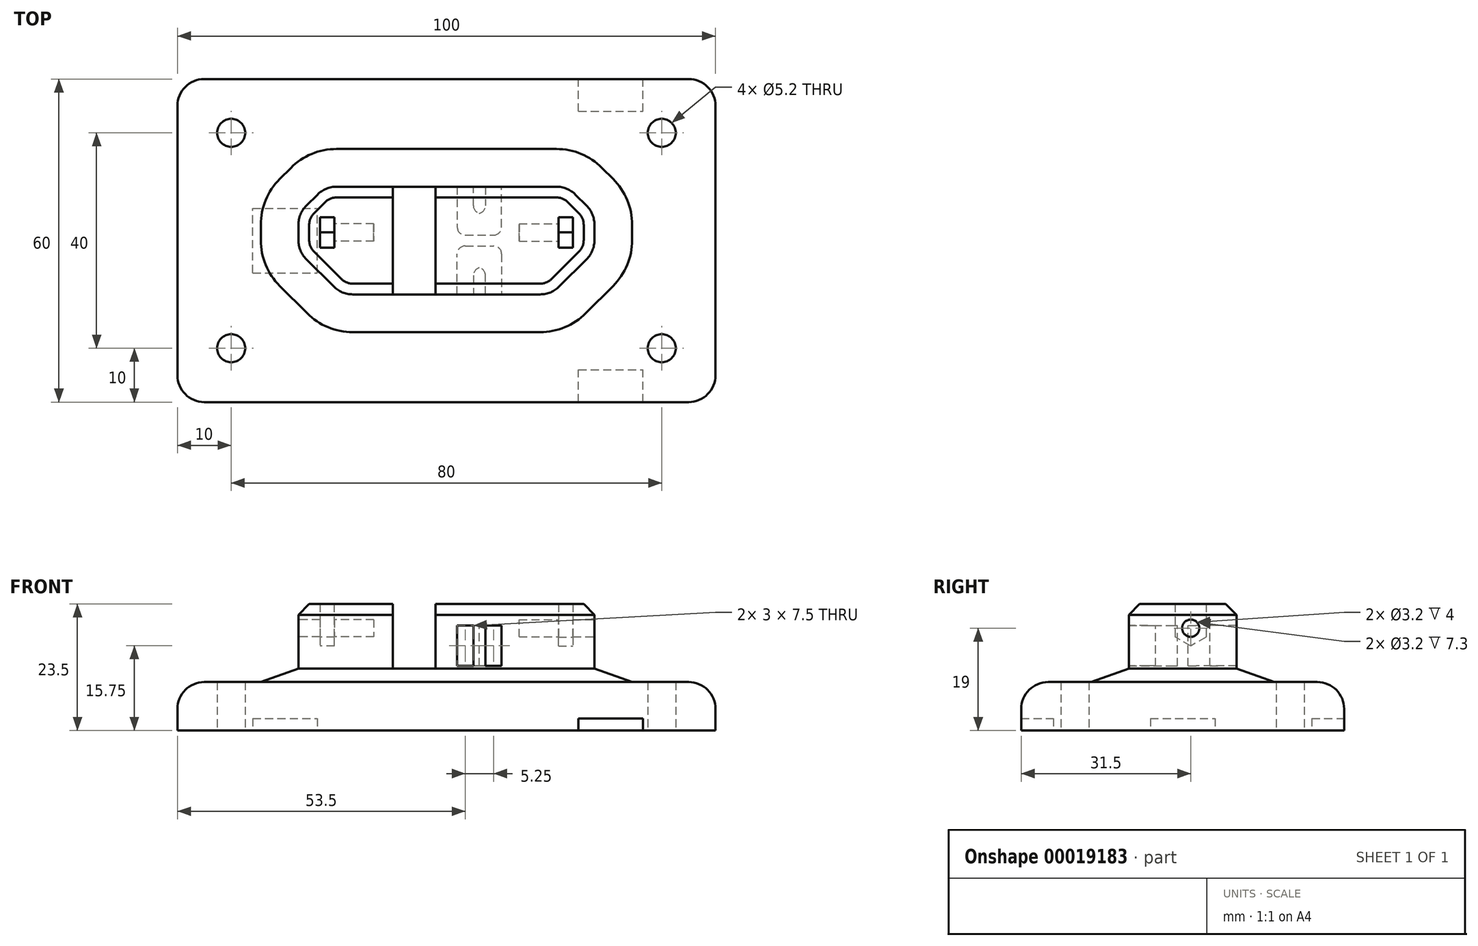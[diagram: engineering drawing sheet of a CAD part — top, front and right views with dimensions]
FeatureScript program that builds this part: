
annotation { "Feature Type Name" : "Feature", "Feature Type Description" : "" }
export const myFeature = defineFeature(function(context is Context, id is Id, definition is map)
    precondition{}
    {
        {
            var Q0;
            Q0=qCreatedBy(makeId("Top.planeOp"),FACE);
            var sketch = newSketch(context, id + "F0", { "sketchPlane" : qUnion([Q0])});
            skLineSegment(sketch, "E0.rect.bottom", {"start": v(-45, 30) * mm, "end": v(45, 30) * mm});
            skLineSegment(sketch, "E0.rect.top", {"start": v(-45, -30) * mm, "end": v(45, -30) * mm});
            skLineSegment(sketch, "E0.rect.left", {"start": v(-50, 25) * mm, "end": v(-50, -25) * mm});
            skLineSegment(sketch, "E0.rect.right", {"start": v(50, 25) * mm, "end": v(50, -25) * mm});
            skPoint(sketch, "E0.rect.middle", {"position": v(0, 0) * mm});
            skCircle(sketch, "E1", {"center": v(-40, 20) * mm, "radius": 2.6 * mm});
            skCircle(sketch, "E2", {"center": v(40, 20) * mm, "radius": 2.6 * mm});
            skCircle(sketch, "E3", {"center": v(40, -20) * mm, "radius": 2.6 * mm});
            skCircle(sketch, "E4", {"center": v(-40, -20) * mm, "radius": 2.6 * mm});
            skPoint(sketch, "E5.visualSharp", {"position": v(-50, 30) * mm});
            skArc(sketch, "E5.filletArc", {"start": v(-45, 30) * mm, "mid": v(-48.54, 28.54) * mm, "end": v(-50, 25) * mm});
            skPoint(sketch, "E6.visualSharp", {"position": v(50, 30) * mm});
            skArc(sketch, "E6.filletArc", {"start": v(50, 25) * mm, "mid": v(48.54, 28.54) * mm, "end": v(45, 30) * mm});
            skPoint(sketch, "E7.visualSharp", {"position": v(50, -30) * mm});
            skArc(sketch, "E7.filletArc", {"start": v(45, -30) * mm, "mid": v(48.54, -28.54) * mm, "end": v(50, -25) * mm});
            skPoint(sketch, "E8.visualSharp", {"position": v(-50, -30) * mm});
            skArc(sketch, "E8.filletArc", {"start": v(-50, -25) * mm, "mid": v(-48.54, -28.54) * mm, "end": v(-45, -30) * mm});
            skSolve(sketch);
        }
        {
            var Q0;
            Q0=qSketchRegion(id+"F0",true);
            extrude(context, id + "F1", {"entities" : qUnion([Q0]), "depth" : 9 * mm});
        }
        {
            var Q0;
            Q0=makeQuery(id+"F1.opExtrude","CAP_FACE",FACE,{"disambiguationData":[OSD([sQuery(id+"F0.wireOp",EDGE,"E0.rect.bottom"),sQuery(id+"F0.wireOp",EDGE,"E0.rect.top"),sQuery(id+"F0.wireOp",EDGE,"E0.rect.left"),sQuery(id+"F0.wireOp",EDGE,"E0.rect.right"),sQuery(id+"F0.wireOp",EDGE,"E1"),sQuery(id+"F0.wireOp",EDGE,"E2"),sQuery(id+"F0.wireOp",EDGE,"E3"),sQuery(id+"F0.wireOp",EDGE,"E4"),sQuery(id+"F0.wireOp",EDGE,"E5.filletArc"),sQuery(id+"F0.wireOp",EDGE,"E6.filletArc"),sQuery(id+"F0.wireOp",EDGE,"E7.filletArc"),sQuery(id+"F0.wireOp",EDGE,"E8.filletArc")])],"isStart":true});
            var sketch = newSketch(context, id + "F2", { "sketchPlane" : qUnion([Q0])});
            skLineSegment(sketch, "E9.rect.bottom", {"start": v(-36, 6) * mm, "end": v(-24, 6) * mm});
            skLineSegment(sketch, "E9.rect.top", {"start": v(-36, -6) * mm, "end": v(-24, -6) * mm});
            skLineSegment(sketch, "E9.rect.left", {"start": v(-36, 6) * mm, "end": v(-36, -6) * mm});
            skLineSegment(sketch, "E9.rect.right", {"start": v(-24, 6) * mm, "end": v(-24, -6) * mm});
            skPoint(sketch, "E9.rect.middle", {"position": v(-30, 0) * mm});
            skLineSegment(sketch, "E10.rect.bottom", {"start": v(24.52, 36) * mm, "end": v(36.52, 36) * mm});
            skLineSegment(sketch, "E10.rect.top", {"start": v(24.52, 24) * mm, "end": v(36.52, 24) * mm});
            skLineSegment(sketch, "E10.rect.left", {"start": v(24.52, 36) * mm, "end": v(24.52, 24) * mm});
            skLineSegment(sketch, "E10.rect.right", {"start": v(36.52, 36) * mm, "end": v(36.52, 24) * mm});
            skPoint(sketch, "E10.rect.middle", {"position": v(30.52, 30) * mm});
            skLineSegment(sketch, "E11.rect.bottom", {"start": v(24.52, -24) * mm, "end": v(36.52, -24) * mm});
            skLineSegment(sketch, "E11.rect.top", {"start": v(24.52, -36) * mm, "end": v(36.52, -36) * mm});
            skLineSegment(sketch, "E11.rect.left", {"start": v(24.52, -24) * mm, "end": v(24.52, -36) * mm});
            skLineSegment(sketch, "E11.rect.right", {"start": v(36.52, -24) * mm, "end": v(36.52, -36) * mm});
            skPoint(sketch, "E11.rect.middle", {"position": v(30.52, -30) * mm});
            skLineSegment(sketch, "E12", {"start": v(0, 0) * mm, "end": v(50, 0) * mm});
            skSolve(sketch);
        }
        {
            var Q0;
            Q0=qSketchRegion(id+"F2",true);
            extrude(context, id + "F3", {"entities" : qUnion([Q0]), "operationType" : NewBodyOperationType.REMOVE, "oppositeDirection" : true, "depth" : 2.25 * mm});
        }
        {
            var Q0;
            Q0=makeQuery(id+"F1.opExtrude","CAP_FACE",FACE,{"disambiguationData":[OSD([sQuery(id+"F0.wireOp",EDGE,"E0.rect.bottom"),sQuery(id+"F0.wireOp",EDGE,"E0.rect.top"),sQuery(id+"F0.wireOp",EDGE,"E0.rect.left"),sQuery(id+"F0.wireOp",EDGE,"E0.rect.right"),sQuery(id+"F0.wireOp",EDGE,"E1"),sQuery(id+"F0.wireOp",EDGE,"E2"),sQuery(id+"F0.wireOp",EDGE,"E3"),sQuery(id+"F0.wireOp",EDGE,"E4"),sQuery(id+"F0.wireOp",EDGE,"E5.filletArc"),sQuery(id+"F0.wireOp",EDGE,"E6.filletArc"),sQuery(id+"F0.wireOp",EDGE,"E7.filletArc"),sQuery(id+"F0.wireOp",EDGE,"E8.filletArc")])],"isStart":false});
            var sketch = newSketch(context, id + "F4", { "sketchPlane" : qUnion([Q0])});
            skPoint(sketch, "E13.orphan", {"position": v(-50, 0) * mm});
            skPoint(sketch, "E14.end.orphan", {"position": v(50, 0) * mm});
            skLineSegment(sketch, "E15.rect.bottom", {"start": v(-27.5, 10) * mm, "end": v(27.5, 10) * mm});
            skLineSegment(sketch, "E15.rect.top", {"start": v(-27.5, -10) * mm, "end": v(27.5, -10) * mm});
            skLineSegment(sketch, "E15.rect.left", {"start": v(-27.5, 10) * mm, "end": v(-27.5, -10) * mm});
            skLineSegment(sketch, "E15.rect.right", {"start": v(27.5, 10) * mm, "end": v(27.5, -10) * mm});
            skPoint(sketch, "E15.rect.middle", {"position": v(0, 0) * mm});
            skSolve(sketch);
        }
        {
            var Q0;
            Q0=qSketchRegion(id+"F4",true);
            extrude(context, id + "F5", {"entities" : qUnion([Q0]), "operationType" : NewBodyOperationType.ADD, "depth" : 14.5 * mm});
        }
        {
            var Q0;
            Q0=makeQuery(id+"F5.opExtrude","SWEPT_EDGE",EDGE,{"disambiguationData":[OSD([sQuery(id+"F4.wireOp",EDGE,"E15.rect.top"),sQuery(id+"F4.wireOp",EDGE,"E15.rect.left")])]});
            var Q1;
            Q1=makeQuery(id+"F5.opExtrude","SWEPT_EDGE",EDGE,{"disambiguationData":[OSD([sQuery(id+"F4.wireOp",EDGE,"E15.rect.top"),sQuery(id+"F4.wireOp",EDGE,"E15.rect.right")])]});
            chamfer(context, id + "F6", {"entities" : qUnion([Q0, Q1]), "width" : 8 * mm, "tangentPropagation" : true});
        }
        {
            var Q0;
            Q0=makeQuery(id+"F5.opExtrude","SWEPT_EDGE",EDGE,{"disambiguationData":[OSD([sQuery(id+"F4.wireOp",EDGE,"E15.rect.bottom"),sQuery(id+"F4.wireOp",EDGE,"E15.rect.left")])]});
            var Q1;
            Q1=makeQuery(id+"F5.opExtrude","SWEPT_EDGE",EDGE,{"disambiguationData":[OSD([sQuery(id+"F4.wireOp",EDGE,"E15.rect.bottom"),sQuery(id+"F4.wireOp",EDGE,"E15.rect.right")])]});
            chamfer(context, id + "F7", {"entities" : qUnion([Q0, Q1]), "width" : 5 * mm, "tangentPropagation" : true});
        }
        {
            var Q0;
            Q0=makeQuery(id+"F5.opExtrude","CAP_FACE",FACE,{"disambiguationData":[OSD([sQuery(id+"F4.wireOp",EDGE,"E15.rect.bottom"),sQuery(id+"F4.wireOp",EDGE,"E15.rect.top"),sQuery(id+"F4.wireOp",EDGE,"E15.rect.left"),sQuery(id+"F4.wireOp",EDGE,"E15.rect.right")])],"isStart":false});
            var sketch = newSketch(context, id + "F8", { "sketchPlane" : qUnion([Q0])});
            skLineSegment(sketch, "E16.rect.bottom", {"start": v(-10, 10) * mm, "end": v(-2, 10) * mm});
            skLineSegment(sketch, "E16.rect.top", {"start": v(-10, -10) * mm, "end": v(-2, -10) * mm});
            skLineSegment(sketch, "E16.rect.left", {"start": v(-10, 10) * mm, "end": v(-10, -10) * mm});
            skLineSegment(sketch, "E16.rect.right", {"start": v(-2, 10) * mm, "end": v(-2, -10) * mm});
            skPoint(sketch, "E16.rect.middle", {"position": v(-6, 0) * mm});
            skSolve(sketch);
        }
        {
            var Q0;
            Q0=qSketchRegion(id+"F8",true);
            extrude(context, id + "F9", {"entities" : qUnion([Q0]), "operationType" : NewBodyOperationType.REMOVE, "oppositeDirection" : true, "depth" : 12 * mm});
        }
        {
            var Q0;
            {var subQ0=sQuery(id+"F4.wireOp",EDGE,"E15.rect.bottom");var subQ1=sQuery(id+"F4.wireOp",EDGE,"E15.rect.top");var subQ2=sQuery(id+"F4.wireOp",EDGE,"E15.rect.right");Q0=makeQuery(id+"F9.boolean.opBoolean","SPLIT",FACE,{"disambiguationData":[TD([makeQuery(id+"F5.opExtrude","SWEPT_FACE",FACE,{"disambiguationData":[OSD([subQ2])]})])],"derivedFrom":makeQuery(id+"F5.opExtrude","CAP_FACE",FACE,{"disambiguationData":[OSD([subQ0,subQ1,sQuery(id+"F4.wireOp",EDGE,"E15.rect.left"),subQ2])],"isStart":false})});}
            cPlane(context, id + "F10", {"entities" : qUnion([Q0]), "cplaneType" : CPlaneType.OFFSET, "offset" : 4 * mm, "oppositeDirection" : true, "width" : 150 * mm, "height" : 150 * mm});
        }
        {
            var Q0;
            Q0=makeQuery(id+"F5.opExtrude","SWEPT_FACE",FACE,{"disambiguationData":[OSD([sQuery(id+"F4.wireOp",EDGE,"E15.rect.left")])]});
            var sketch = newSketch(context, id + "F11", { "sketchPlane" : qUnion([Q0])});
            skCircle(sketch, "E17", {"center": v(-1.5, 19) * mm, "radius": 1.6 * mm});
            skSolve(sketch);
        }
        {
            var Q0;
            Q0=qSketchRegion(id+"F11",true);
            extrude(context, id + "F12", {"entities" : qUnion([Q0]), "operationType" : NewBodyOperationType.REMOVE, "oppositeDirection" : true, "depth" : 14 * mm});
        }
        {
            var Q0;
            Q0=makeQuery(id+"F5.opExtrude","SWEPT_FACE",FACE,{"disambiguationData":[OSD([sQuery(id+"F4.wireOp",EDGE,"E15.rect.right")])]});
            var sketch = newSketch(context, id + "F13", { "sketchPlane" : qUnion([Q0])});
            skCircle(sketch, "E18", {"center": v(1.5, 19) * mm, "radius": 1.6 * mm});
            skSolve(sketch);
        }
        {
            var Q0;
            Q0=qSketchRegion(id+"F13",true);
            extrude(context, id + "F14", {"entities" : qUnion([Q0]), "operationType" : NewBodyOperationType.REMOVE, "oppositeDirection" : true, "depth" : 14 * mm});
        }
        {
            var Q0;
            Q0=qCreatedBy(id+"F10.planeOp",FACE);
            var sketch = newSketch(context, id + "F15", { "sketchPlane" : qUnion([Q0])});
            skLineSegment(sketch, "E19", {"start": v(2, -10) * mm, "end": v(2, -1) * mm});
            skLineSegment(sketch, "E20", {"start": v(2, -1) * mm, "end": v(10.25, -1) * mm});
            skLineSegment(sketch, "E21", {"start": v(10.25, -1) * mm, "end": v(10.25, -10) * mm});
            skLineSegment(sketch, "E22", {"start": v(10.25, -10) * mm, "end": v(7.25, -10) * mm});
            skLineSegment(sketch, "E23", {"start": v(7.25, -10) * mm, "end": v(7.25, -5) * mm});
            skLineSegment(sketch, "E24", {"start": v(7.25, -5) * mm, "end": v(5, -5) * mm});
            skLineSegment(sketch, "E25", {"start": v(5, -5) * mm, "end": v(5, -10) * mm});
            skLineSegment(sketch, "E26", {"start": v(5, -10) * mm, "end": v(2, -10) * mm});
            skLineSegment(sketch, "E27", {"start": v(2, 10) * mm, "end": v(2, 1) * mm});
            skLineSegment(sketch, "E28", {"start": v(2, 1) * mm, "end": v(10.25, 1) * mm});
            skLineSegment(sketch, "E29", {"start": v(10.25, 1) * mm, "end": v(10.25, 10) * mm});
            skLineSegment(sketch, "E30", {"start": v(10.25, 10) * mm, "end": v(7.25, 10) * mm});
            skLineSegment(sketch, "E31", {"start": v(7.25, 10) * mm, "end": v(7.25, 5) * mm});
            skLineSegment(sketch, "E32", {"start": v(7.25, 5) * mm, "end": v(5, 5) * mm});
            skLineSegment(sketch, "E33", {"start": v(5, 5) * mm, "end": v(5, 10) * mm});
            skLineSegment(sketch, "E34", {"start": v(5, 10) * mm, "end": v(2, 10) * mm});
            skSolve(sketch);
        }
        {
            var Q0;
            Q0=qSketchRegion(id+"F15",true);
            extrude(context, id + "F16", {"entities" : qUnion([Q0]), "operationType" : NewBodyOperationType.REMOVE, "oppositeDirection" : true, "depth" : 7.5 * mm});
        }
        {
            var Q0;
            Q0=makeQuery(id+"F16.boolean.opBoolean","COPY",EDGE,{"derivedFrom":makeQuery(id+"F16.opExtrude","SWEPT_EDGE",EDGE,{"disambiguationData":[OSD([sQuery(id+"F15.wireOp",EDGE,"E23"),sQuery(id+"F15.wireOp",EDGE,"E24")])]})});
            var Q1;
            Q1=makeQuery(id+"F16.boolean.opBoolean","COPY",EDGE,{"derivedFrom":makeQuery(id+"F16.opExtrude","SWEPT_EDGE",EDGE,{"disambiguationData":[OSD([sQuery(id+"F15.wireOp",EDGE,"E24"),sQuery(id+"F15.wireOp",EDGE,"E25")])]})});
            var Q2;
            Q2=makeQuery(id+"F16.boolean.opBoolean","COPY",EDGE,{"derivedFrom":makeQuery(id+"F16.opExtrude","SWEPT_EDGE",EDGE,{"disambiguationData":[OSD([sQuery(id+"F15.wireOp",EDGE,"E19"),sQuery(id+"F15.wireOp",EDGE,"E20")])]})});
            var Q3;
            Q3=makeQuery(id+"F16.boolean.opBoolean","COPY",EDGE,{"derivedFrom":makeQuery(id+"F16.opExtrude","SWEPT_EDGE",EDGE,{"disambiguationData":[OSD([sQuery(id+"F15.wireOp",EDGE,"E20"),sQuery(id+"F15.wireOp",EDGE,"E21")])]})});
            var Q4;
            Q4=makeQuery(id+"F16.boolean.opBoolean","COPY",EDGE,{"derivedFrom":makeQuery(id+"F16.opExtrude","SWEPT_EDGE",EDGE,{"disambiguationData":[OSD([sQuery(id+"F15.wireOp",EDGE,"E32"),sQuery(id+"F15.wireOp",EDGE,"E33")])]})});
            var Q5;
            Q5=makeQuery(id+"F16.boolean.opBoolean","COPY",EDGE,{"derivedFrom":makeQuery(id+"F16.opExtrude","SWEPT_EDGE",EDGE,{"disambiguationData":[OSD([sQuery(id+"F15.wireOp",EDGE,"E31"),sQuery(id+"F15.wireOp",EDGE,"E32")])]})});
            var Q6;
            Q6=makeQuery(id+"F16.boolean.opBoolean","COPY",EDGE,{"derivedFrom":makeQuery(id+"F16.opExtrude","SWEPT_EDGE",EDGE,{"disambiguationData":[OSD([sQuery(id+"F15.wireOp",EDGE,"E27"),sQuery(id+"F15.wireOp",EDGE,"E28")])]})});
            var Q7;
            Q7=makeQuery(id+"F16.boolean.opBoolean","COPY",EDGE,{"derivedFrom":makeQuery(id+"F16.opExtrude","SWEPT_EDGE",EDGE,{"disambiguationData":[OSD([sQuery(id+"F15.wireOp",EDGE,"E28"),sQuery(id+"F15.wireOp",EDGE,"E29")])]})});
            fillet(context, id + "F17", {"entities" : qUnion([Q0, Q1, Q2, Q3, Q4, Q5, Q6, Q7]), "radius" : 1.5 * mm, "tangentPropagation" : true, "allowEdgeOverflow" : false});
        }
        {
            var Q0;
            Q0=makeQuery(id+"F5.opExtrude","SWEPT_FACE",FACE,{"disambiguationData":[OSD([sQuery(id+"F4.wireOp",EDGE,"E15.rect.right")])]});
            cPlane(context, id + "F18", {"entities" : qUnion([Q0]), "cplaneType" : CPlaneType.OFFSET, "offset" : 4 * mm, "oppositeDirection" : true, "width" : 150 * mm, "height" : 150 * mm});
        }
        {
            var Q0;
            Q0=qCreatedBy(id+"F18.planeOp",FACE);
            var sketch = newSketch(context, id + "F19", { "sketchPlane" : qUnion([Q0])});
            skCircle(sketch, "E35.cCircle", {"center": v(1.5, 19) * mm, "radius": 2.85 * mm, "construction": true});
            skLineSegment(sketch, "E35.0", {"start": v(-1.35, 17.35) * mm, "end": v(-1.35, 20.65) * mm});
            skLineSegment(sketch, "E35.1", {"start": v(-1.35, 20.65) * mm, "end": v(1.5, 22.3) * mm});
            skLineSegment(sketch, "E35.2", {"start": v(1.5, 22.3) * mm, "end": v(4.35, 20.65) * mm});
            skLineSegment(sketch, "E35.3", {"start": v(4.35, 20.65) * mm, "end": v(4.35, 17.35) * mm});
            skLineSegment(sketch, "E35.4", {"start": v(4.35, 17.35) * mm, "end": v(1.5, 15.7) * mm});
            skLineSegment(sketch, "E35.5", {"start": v(1.5, 15.7) * mm, "end": v(-1.35, 17.35) * mm});
            skPoint(sketch, "E35.0.midPoint", {"position": v(-1.35, 19) * mm});
            skLineSegment(sketch, "E36", {"start": v(-1.35, 20.65) * mm, "end": v(-1.35, 23.5) * mm});
            skLineSegment(sketch, "E37", {"start": v(-1.35, 23.5) * mm, "end": v(4.35, 23.5) * mm});
            skLineSegment(sketch, "E38", {"start": v(4.35, 23.5) * mm, "end": v(4.35, 20.65) * mm});
            skSolve(sketch);
        }
        {
            var Q0;
            Q0=qSketchRegion(id+"F19",true);
            extrude(context, id + "F20", {"entities" : qUnion([Q0]), "operationType" : NewBodyOperationType.REMOVE, "oppositeDirection" : true, "depth" : 2.7 * mm});
        }
        {
            var Q0;
            Q0=makeQuery(id+"F5.opExtrude","SWEPT_FACE",FACE,{"disambiguationData":[OSD([sQuery(id+"F4.wireOp",EDGE,"E15.rect.left")])]});
            cPlane(context, id + "F21", {"entities" : qUnion([Q0]), "cplaneType" : CPlaneType.OFFSET, "offset" : 4 * mm, "oppositeDirection" : true, "width" : 150 * mm, "height" : 150 * mm});
        }
        {
            var Q0;
            Q0=qCreatedBy(id+"F21.planeOp",FACE);
            var sketch = newSketch(context, id + "F22", { "sketchPlane" : qUnion([Q0])});
            skCircle(sketch, "E39.cCircle", {"center": v(-1.5, 19) * mm, "radius": 2.85 * mm, "construction": true});
            skLineSegment(sketch, "E39.0", {"start": v(-4.35, 20.65) * mm, "end": v(-1.5, 22.3) * mm});
            skLineSegment(sketch, "E39.1", {"start": v(-1.5, 22.3) * mm, "end": v(1.35, 20.65) * mm});
            skLineSegment(sketch, "E39.2", {"start": v(1.35, 20.65) * mm, "end": v(1.35, 17.35) * mm});
            skLineSegment(sketch, "E39.3", {"start": v(1.35, 17.35) * mm, "end": v(-1.5, 15.7) * mm});
            skLineSegment(sketch, "E39.4", {"start": v(-1.5, 15.7) * mm, "end": v(-4.35, 17.35) * mm});
            skLineSegment(sketch, "E39.5", {"start": v(-4.35, 17.35) * mm, "end": v(-4.35, 20.65) * mm});
            skPoint(sketch, "E39.0.midPoint", {"position": v(-2.92, 21.47) * mm});
            skLineSegment(sketch, "E40", {"start": v(-4.35, 20.65) * mm, "end": v(-4.35, 23.5) * mm});
            skLineSegment(sketch, "E41", {"start": v(-4.35, 23.5) * mm, "end": v(1.35, 23.5) * mm});
            skLineSegment(sketch, "E42", {"start": v(1.35, 23.5) * mm, "end": v(1.35, 20.65) * mm});
            skSolve(sketch);
        }
        {
            var Q0;
            Q0=qSketchRegion(id+"F22",true);
            extrude(context, id + "F23", {"entities" : qUnion([Q0]), "operationType" : NewBodyOperationType.REMOVE, "oppositeDirection" : true, "depth" : 2.7 * mm});
        }
        {
            var Q0;
            Q0=makeQuery(id+"F1.opExtrude","CAP_EDGE",EDGE,{"disambiguationData":[OSD([sQuery(id+"F0.wireOp",EDGE,"E0.rect.top")])],"isStart":false});
            fillet(context, id + "F24", {"entities" : qUnion([Q0]), "radius" : 5 * mm, "tangentPropagation" : true, "allowEdgeOverflow" : false});
        }
        {
            var Q0;
            {var subQ0=sQuery(id+"F4.wireOp",EDGE,"E15.rect.top");Q0=makeQuery(id+"F6.opChamfer","BLEND_EDGE",EDGE,{"blendedFrom":[makeQuery(id+"F5.opExtrude","SWEPT_EDGE",EDGE,{"disambiguationData":[OSD([subQ0,sQuery(id+"F4.wireOp",EDGE,"E15.rect.left")])]}),makeQuery(id+"F5.opExtrude","SWEPT_FACE",FACE,{"disambiguationData":[OSD([subQ0])]})],"blendedInto":[makeQuery(id+"F5.opExtrude","SWEPT_FACE",FACE,{"disambiguationData":[OSD([subQ0])]})]});}
            var Q1;
            {var subQ0=sQuery(id+"F4.wireOp",EDGE,"E15.rect.left");Q1=makeQuery(id+"F6.opChamfer","BLEND_EDGE",EDGE,{"blendedFrom":[makeQuery(id+"F5.opExtrude","SWEPT_EDGE",EDGE,{"disambiguationData":[OSD([sQuery(id+"F4.wireOp",EDGE,"E15.rect.top"),subQ0])]}),makeQuery(id+"F5.opExtrude","SWEPT_FACE",FACE,{"disambiguationData":[OSD([subQ0])]})],"blendedInto":[makeQuery(id+"F5.opExtrude","SWEPT_FACE",FACE,{"disambiguationData":[OSD([subQ0])]})]});}
            var Q2;
            {var subQ0=sQuery(id+"F4.wireOp",EDGE,"E15.rect.left");Q2=makeQuery(id+"F7.opChamfer","BLEND_EDGE",EDGE,{"blendedFrom":[makeQuery(id+"F5.opExtrude","SWEPT_EDGE",EDGE,{"disambiguationData":[OSD([sQuery(id+"F4.wireOp",EDGE,"E15.rect.bottom"),subQ0])]}),makeQuery(id+"F5.opExtrude","SWEPT_FACE",FACE,{"disambiguationData":[OSD([subQ0])]})],"blendedInto":[makeQuery(id+"F5.opExtrude","SWEPT_FACE",FACE,{"disambiguationData":[OSD([subQ0])]})]});}
            var Q3;
            {var subQ0=sQuery(id+"F4.wireOp",EDGE,"E15.rect.bottom");Q3=makeQuery(id+"F7.opChamfer","BLEND_EDGE",EDGE,{"blendedFrom":[makeQuery(id+"F5.opExtrude","SWEPT_EDGE",EDGE,{"disambiguationData":[OSD([subQ0,sQuery(id+"F4.wireOp",EDGE,"E15.rect.left")])]}),makeQuery(id+"F5.opExtrude","SWEPT_FACE",FACE,{"disambiguationData":[OSD([subQ0])]})],"blendedInto":[makeQuery(id+"F5.opExtrude","SWEPT_FACE",FACE,{"disambiguationData":[OSD([subQ0])]})]});}
            var Q4;
            Q4=makeQuery(id+"F9.boolean.opBoolean","COPY",EDGE,{"derivedFrom":makeQuery(id+"F9.opExtrude","SWEPT_EDGE",EDGE,{"disambiguationData":[OSD([sQuery(id+"F4.wireOp",EDGE,"E15.rect.top"),sQuery(id+"F8.wireOp",EDGE,"E16.rect.top"),sQuery(id+"F8.wireOp",EDGE,"E16.rect.left")])]})});
            var Q5;
            Q5=makeQuery(id+"F9.boolean.opBoolean","COPY",EDGE,{"derivedFrom":makeQuery(id+"F9.opExtrude","SWEPT_EDGE",EDGE,{"disambiguationData":[OSD([sQuery(id+"F4.wireOp",EDGE,"E15.rect.bottom"),sQuery(id+"F8.wireOp",EDGE,"E16.rect.bottom"),sQuery(id+"F8.wireOp",EDGE,"E16.rect.left")])]})});
            var Q6;
            Q6=makeQuery(id+"F9.boolean.opBoolean","COPY",EDGE,{"derivedFrom":makeQuery(id+"F9.opExtrude","SWEPT_EDGE",EDGE,{"disambiguationData":[OSD([sQuery(id+"F4.wireOp",EDGE,"E15.rect.bottom"),sQuery(id+"F8.wireOp",EDGE,"E16.rect.bottom"),sQuery(id+"F8.wireOp",EDGE,"E16.rect.right")])]})});
            var Q7;
            Q7=makeQuery(id+"F9.boolean.opBoolean","COPY",EDGE,{"derivedFrom":makeQuery(id+"F9.opExtrude","SWEPT_EDGE",EDGE,{"disambiguationData":[OSD([sQuery(id+"F4.wireOp",EDGE,"E15.rect.top"),sQuery(id+"F8.wireOp",EDGE,"E16.rect.top"),sQuery(id+"F8.wireOp",EDGE,"E16.rect.right")])]})});
            var Q8;
            {var subQ0=sQuery(id+"F4.wireOp",EDGE,"E15.rect.top");Q8=makeQuery(id+"F6.opChamfer","BLEND_EDGE",EDGE,{"blendedFrom":[makeQuery(id+"F5.opExtrude","SWEPT_EDGE",EDGE,{"disambiguationData":[OSD([subQ0,sQuery(id+"F4.wireOp",EDGE,"E15.rect.right")])]}),makeQuery(id+"F5.opExtrude","SWEPT_FACE",FACE,{"disambiguationData":[OSD([subQ0])]})],"blendedInto":[makeQuery(id+"F5.opExtrude","SWEPT_FACE",FACE,{"disambiguationData":[OSD([subQ0])]})]});}
            var Q9;
            {var subQ0=sQuery(id+"F4.wireOp",EDGE,"E15.rect.right");Q9=makeQuery(id+"F6.opChamfer","BLEND_EDGE",EDGE,{"blendedFrom":[makeQuery(id+"F5.opExtrude","SWEPT_EDGE",EDGE,{"disambiguationData":[OSD([sQuery(id+"F4.wireOp",EDGE,"E15.rect.top"),subQ0])]}),makeQuery(id+"F5.opExtrude","SWEPT_FACE",FACE,{"disambiguationData":[OSD([subQ0])]})],"blendedInto":[makeQuery(id+"F5.opExtrude","SWEPT_FACE",FACE,{"disambiguationData":[OSD([subQ0])]})]});}
            var Q10;
            {var subQ0=sQuery(id+"F4.wireOp",EDGE,"E15.rect.right");Q10=makeQuery(id+"F7.opChamfer","BLEND_EDGE",EDGE,{"blendedFrom":[makeQuery(id+"F5.opExtrude","SWEPT_EDGE",EDGE,{"disambiguationData":[OSD([sQuery(id+"F4.wireOp",EDGE,"E15.rect.bottom"),subQ0])]}),makeQuery(id+"F5.opExtrude","SWEPT_FACE",FACE,{"disambiguationData":[OSD([subQ0])]})],"blendedInto":[makeQuery(id+"F5.opExtrude","SWEPT_FACE",FACE,{"disambiguationData":[OSD([subQ0])]})]});}
            var Q11;
            {var subQ0=sQuery(id+"F4.wireOp",EDGE,"E15.rect.bottom");Q11=makeQuery(id+"F7.opChamfer","BLEND_EDGE",EDGE,{"blendedFrom":[makeQuery(id+"F5.opExtrude","SWEPT_EDGE",EDGE,{"disambiguationData":[OSD([subQ0,sQuery(id+"F4.wireOp",EDGE,"E15.rect.right")])]}),makeQuery(id+"F5.opExtrude","SWEPT_FACE",FACE,{"disambiguationData":[OSD([subQ0])]})],"blendedInto":[makeQuery(id+"F5.opExtrude","SWEPT_FACE",FACE,{"disambiguationData":[OSD([subQ0])]})]});}
            fillet(context, id + "F25", {"entities" : qUnion([Q0, Q1, Q2, Q3, Q4, Q5, Q6, Q7, Q8, Q9, Q10, Q11]), "radius" : 5 * mm, "tangentPropagation" : true, "allowEdgeOverflow" : false});
        }
        {
            var Q0;
            Q0=makeQuery(id+"F5.opExtrude","CAP_EDGE",EDGE,{"disambiguationData":[OSD([sQuery(id+"F4.wireOp",EDGE,"E15.rect.left")])],"isStart":false});
            var Q1;
            Q1=makeQuery(id+"F5.opExtrude","CAP_EDGE",EDGE,{"disambiguationData":[OSD([sQuery(id+"F4.wireOp",EDGE,"E15.rect.right")])],"isStart":false});
            chamfer(context, id + "F26", {"entities" : qUnion([Q0, Q1]), "width" : 2 * mm, "tangentPropagation" : true});
        }
        {
            var Q0;
            Q0=makeQuery(id+"F6.opChamfer","BLEND_EDGE",EDGE,{"blendedFrom":[makeQuery(id+"F5.opExtrude","SWEPT_EDGE",EDGE,{"disambiguationData":[OSD([sQuery(id+"F4.wireOp",EDGE,"E15.rect.top"),sQuery(id+"F4.wireOp",EDGE,"E15.rect.left")])]}),makeQuery(id+"F1.opExtrude","CAP_FACE",FACE,{"disambiguationData":[OSD([sQuery(id+"F0.wireOp",EDGE,"E0.rect.bottom"),sQuery(id+"F0.wireOp",EDGE,"E0.rect.top"),sQuery(id+"F0.wireOp",EDGE,"E0.rect.left"),sQuery(id+"F0.wireOp",EDGE,"E0.rect.right"),sQuery(id+"F0.wireOp",EDGE,"E1"),sQuery(id+"F0.wireOp",EDGE,"E2"),sQuery(id+"F0.wireOp",EDGE,"E3"),sQuery(id+"F0.wireOp",EDGE,"E4"),sQuery(id+"F0.wireOp",EDGE,"E5.filletArc"),sQuery(id+"F0.wireOp",EDGE,"E6.filletArc"),sQuery(id+"F0.wireOp",EDGE,"E7.filletArc"),sQuery(id+"F0.wireOp",EDGE,"E8.filletArc")])],"isStart":false})],"blendedInto":[makeQuery(id+"F1.opExtrude","CAP_FACE",FACE,{"disambiguationData":[OSD([sQuery(id+"F0.wireOp",EDGE,"E0.rect.bottom"),sQuery(id+"F0.wireOp",EDGE,"E0.rect.top"),sQuery(id+"F0.wireOp",EDGE,"E0.rect.left"),sQuery(id+"F0.wireOp",EDGE,"E0.rect.right"),sQuery(id+"F0.wireOp",EDGE,"E1"),sQuery(id+"F0.wireOp",EDGE,"E2"),sQuery(id+"F0.wireOp",EDGE,"E3"),sQuery(id+"F0.wireOp",EDGE,"E4"),sQuery(id+"F0.wireOp",EDGE,"E5.filletArc"),sQuery(id+"F0.wireOp",EDGE,"E6.filletArc"),sQuery(id+"F0.wireOp",EDGE,"E7.filletArc"),sQuery(id+"F0.wireOp",EDGE,"E8.filletArc")])],"isStart":false})]});
            chamfer(context, id + "F27", {"entities" : qUnion([Q0]), "chamferType" : ChamferType.TWO_OFFSETS, "width1" : 7 * mm, "oppositeDirection" : false, "width2" : 2.5 * mm, "tangentPropagation" : true});
        }
    });
